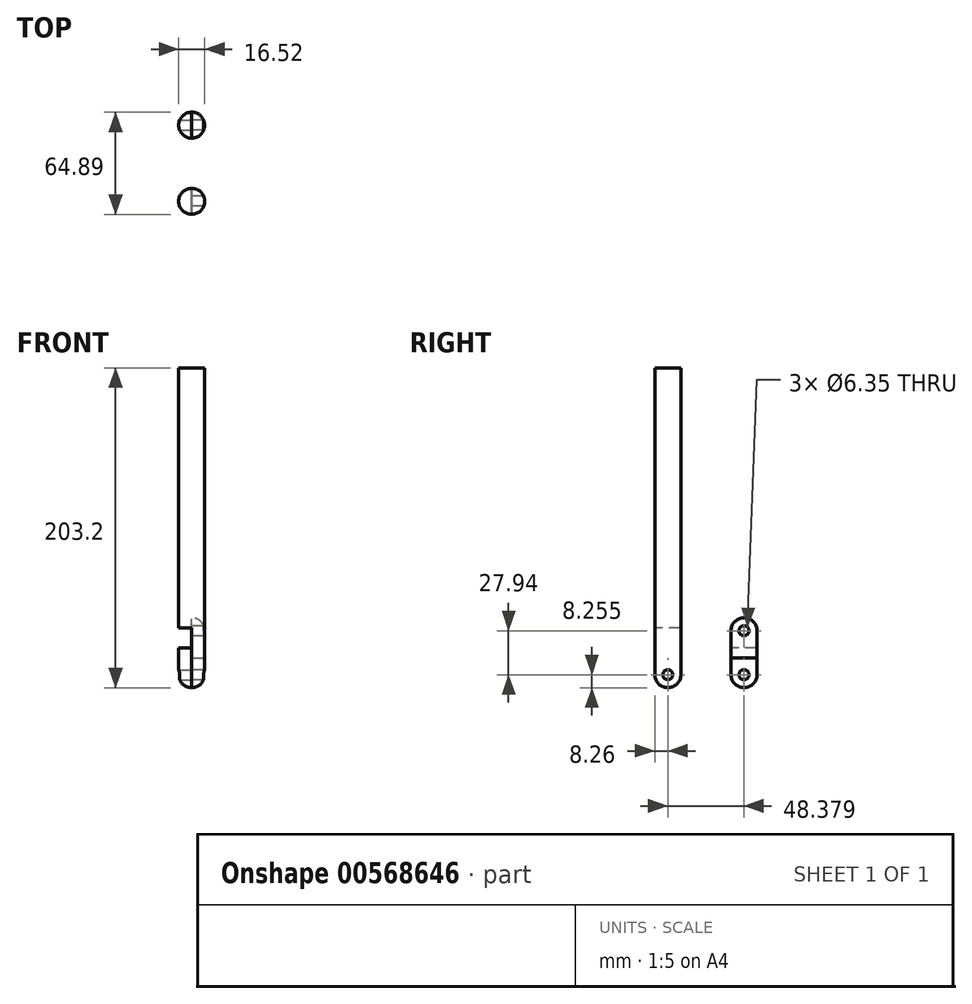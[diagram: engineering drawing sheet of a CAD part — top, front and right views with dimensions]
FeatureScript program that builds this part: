
annotation { "Feature Type Name" : "Feature", "Feature Type Description" : "" }
export const myFeature = defineFeature(function(context is Context, id is Id, definition is map)
    precondition{}
    {
        {
            var Q0;
            Q0=qCreatedBy(makeId("Top.planeOp"),FACE);
            var sketch = newSketch(context, id + "F0", { "sketchPlane" : qUnion([Q0])});
            skCircle(sketch, "E0", {"center": v(0, 0) * mm, "radius": 8.26 * mm});
            skSolve(sketch);
        }
        {
            var Q0;
            Q0 = qSketchRegion(id + "F0", true);
            extrude(context, id + "F1", {"entities" : qUnion([Q0]), "depth" : 203.2 * mm, "offsetDistance" : 25.4 * mm});
        }
        {
            var Q0;
            Q0=makeQuery(id+"F1.opExtrude","CAP_EDGE",EDGE,{"disambiguationData":[OSD([sQuery(id+"F0.wireOp",EDGE,"E0")])],"isStart":true});
            fillet(context, id + "F2", {"entities" : qUnion([Q0]), "radius" : 8.25 * mm, "tangentPropagation" : true, "allowEdgeOverflow" : false});
        }
        {
            var Q0;
            Q0=qCreatedBy(makeId("Right.planeOp"),FACE);
            var sketch = newSketch(context, id + "F3", { "sketchPlane" : qUnion([Q0])});
            skLineSegment(sketch, "E1.bottom", {"start": v(29.47, 38.1) * mm, "end": v(-36.1, 38.1) * mm});
            skLineSegment(sketch, "E1.top", {"start": v(29.47, -29.7) * mm, "end": v(-36.1, -29.7) * mm});
            skLineSegment(sketch, "E1.left", {"start": v(29.47, 38.1) * mm, "end": v(29.47, -29.7) * mm});
            skLineSegment(sketch, "E1.right", {"start": v(-36.1, 38.1) * mm, "end": v(-36.1, -29.7) * mm});
            skSolve(sketch);
        }
        {
            var Q0;
            Q0 = qSketchRegion(id + "F3", true);
            extrude(context, id + "F4", {"entities" : qUnion([Q0]), "operationType" : NewBodyOperationType.REMOVE, "oppositeDirection" : true, "depth" : 25.4 * mm, "offsetDistance" : 25.4 * mm});
        }
        {
            var Q0;
            Q0=makeQuery(id+"F4.boolean.opBoolean","COPY",FACE,{"derivedFrom":makeQuery(id+"F4.opExtrude","CAP_FACE",FACE,{"disambiguationData":[OSD([sQuery(id+"F3.wireOp",EDGE,"E1.bottom"),sQuery(id+"F3.wireOp",EDGE,"E1.top"),sQuery(id+"F3.wireOp",EDGE,"E1.left"),sQuery(id+"F3.wireOp",EDGE,"E1.right")])],"isStart":true})});
            var sketch = newSketch(context, id + "F5", { "sketchPlane" : qUnion([Q0])});
            skCircle(sketch, "E2", {"center": v(0, 8.26) * mm, "radius": 3.18 * mm});
            skSolve(sketch);
        }
        {
            var Q0;
            Q0 = qSketchRegion(id + "F5", true);
            extrude(context, id + "F6", {"entities" : qUnion([Q0]), "operationType" : NewBodyOperationType.REMOVE, "oppositeDirection" : true, "depth" : 25.4 * mm, "offsetDistance" : 25.4 * mm});
        }
        {
            var Q0;
            Q0=qCreatedBy(makeId("Top.planeOp"),FACE);
            var sketch = newSketch(context, id + "F7", { "sketchPlane" : qUnion([Q0])});
            skCircle(sketch, "E3", {"center": v(0, 48.38) * mm, "radius": 8.26 * mm});
            skSolve(sketch);
        }
        {
            var Q0;
            Q0 = qSketchRegion(id + "F7", true);
            extrude(context, id + "F8", {"entities" : qUnion([Q0]), "depth" : 44.45 * mm, "offsetDistance" : 25.4 * mm});
        }
        {
            var Q0;
            Q0=qCreatedBy(makeId("Right.planeOp"),FACE);
            var sketch = newSketch(context, id + "F9", { "sketchPlane" : qUnion([Q0])});
            skLineSegment(sketch, "E4.bottom", {"start": v(63.14, 50.1) * mm, "end": v(34.58, 50.1) * mm});
            skLineSegment(sketch, "E4.top", {"start": v(63.14, 25.4) * mm, "end": v(34.58, 25.4) * mm});
            skLineSegment(sketch, "E4.left", {"start": v(63.14, 50.1) * mm, "end": v(63.14, 25.4) * mm});
            skLineSegment(sketch, "E4.right", {"start": v(34.58, 50.1) * mm, "end": v(34.58, 25.4) * mm});
            skSolve(sketch);
        }
        {
            var Q0;
            Q0 = qSketchRegion(id + "F9", true);
            extrude(context, id + "F10", {"entities" : qUnion([Q0]), "operationType" : NewBodyOperationType.REMOVE, "oppositeDirection" : true, "depth" : 25.4 * mm, "offsetDistance" : 25.4 * mm});
        }
        {
            var Q0;
            Q0=makeQuery(id+"F8.opExtrude","CAP_EDGE",EDGE,{"disambiguationData":[OSD([sQuery(id+"F7.wireOp",EDGE,"E3")])],"isStart":false});
            fillet(context, id + "F11", {"entities" : qUnion([Q0]), "radius" : 8.25 * mm, "tangentPropagation" : true, "allowEdgeOverflow" : false});
        }
        {
            var Q0;
            Q0=makeQuery(id+"F10.boolean.opBoolean","COPY",FACE,{"derivedFrom":makeQuery(id+"F10.opExtrude","CAP_FACE",FACE,{"disambiguationData":[OSD([sQuery(id+"F9.wireOp",EDGE,"E4.bottom"),sQuery(id+"F9.wireOp",EDGE,"E4.top"),sQuery(id+"F9.wireOp",EDGE,"E4.left"),sQuery(id+"F9.wireOp",EDGE,"E4.right")])],"isStart":true})});
            var sketch = newSketch(context, id + "F12", { "sketchPlane" : qUnion([Q0])});
            skCircle(sketch, "E5", {"center": v(-48.38, 36.2) * mm, "radius": 3.18 * mm});
            skSolve(sketch);
        }
        {
            var Q0;
            Q0 = qSketchRegion(id + "F12", true);
            extrude(context, id + "F13", {"entities" : qUnion([Q0]), "operationType" : NewBodyOperationType.REMOVE, "oppositeDirection" : true, "depth" : 25.4 * mm, "offsetDistance" : 25.4 * mm});
        }
        {
            var Q0;
            Q0=qCreatedBy(makeId("Right.planeOp"),FACE);
            var sketch = newSketch(context, id + "F14", { "sketchPlane" : qUnion([Q0])});
            skLineSegment(sketch, "E6.bottom", {"start": v(66.56, -10.27) * mm, "end": v(32.1, -10.27) * mm});
            skLineSegment(sketch, "E6.top", {"start": v(66.56, 19.05) * mm, "end": v(32.1, 19.05) * mm});
            skLineSegment(sketch, "E6.left", {"start": v(66.56, -10.27) * mm, "end": v(66.56, 19.05) * mm});
            skLineSegment(sketch, "E6.right", {"start": v(32.1, -10.27) * mm, "end": v(32.1, 19.05) * mm});
            skSolve(sketch);
        }
        {
            var Q0;
            Q0 = qSketchRegion(id + "F14", true);
            extrude(context, id + "F15", {"entities" : qUnion([Q0]), "operationType" : NewBodyOperationType.REMOVE, "depth" : 25.4 * mm, "offsetDistance" : 25.4 * mm});
        }
        {
            var Q0;
            Q0=makeQuery(id+"F8.opExtrude","CAP_EDGE",EDGE,{"disambiguationData":[OSD([sQuery(id+"F7.wireOp",EDGE,"E3")])],"isStart":true});
            fillet(context, id + "F16", {"entities" : qUnion([Q0]), "radius" : 8.25 * mm, "tangentPropagation" : true, "allowEdgeOverflow" : false});
        }
        {
            var Q0;
            Q0=makeQuery(id+"F15.boolean.opBoolean","COPY",FACE,{"derivedFrom":makeQuery(id+"F15.opExtrude","CAP_FACE",FACE,{"disambiguationData":[OSD([sQuery(id+"F14.wireOp",EDGE,"E6.bottom"),sQuery(id+"F14.wireOp",EDGE,"E6.top"),sQuery(id+"F14.wireOp",EDGE,"E6.left"),sQuery(id+"F14.wireOp",EDGE,"E6.right")])],"isStart":true})});
            var sketch = newSketch(context, id + "F17", { "sketchPlane" : qUnion([Q0])});
            skCircle(sketch, "E7", {"center": v(48.38, 8.25) * mm, "radius": 3.18 * mm});
            skSolve(sketch);
        }
        {
            var Q0;
            Q0 = qSketchRegion(id + "F17", true);
            extrude(context, id + "F18", {"entities" : qUnion([Q0]), "operationType" : NewBodyOperationType.REMOVE, "oppositeDirection" : true, "depth" : 25.4 * mm, "offsetDistance" : 25.4 * mm});
        }
    });
